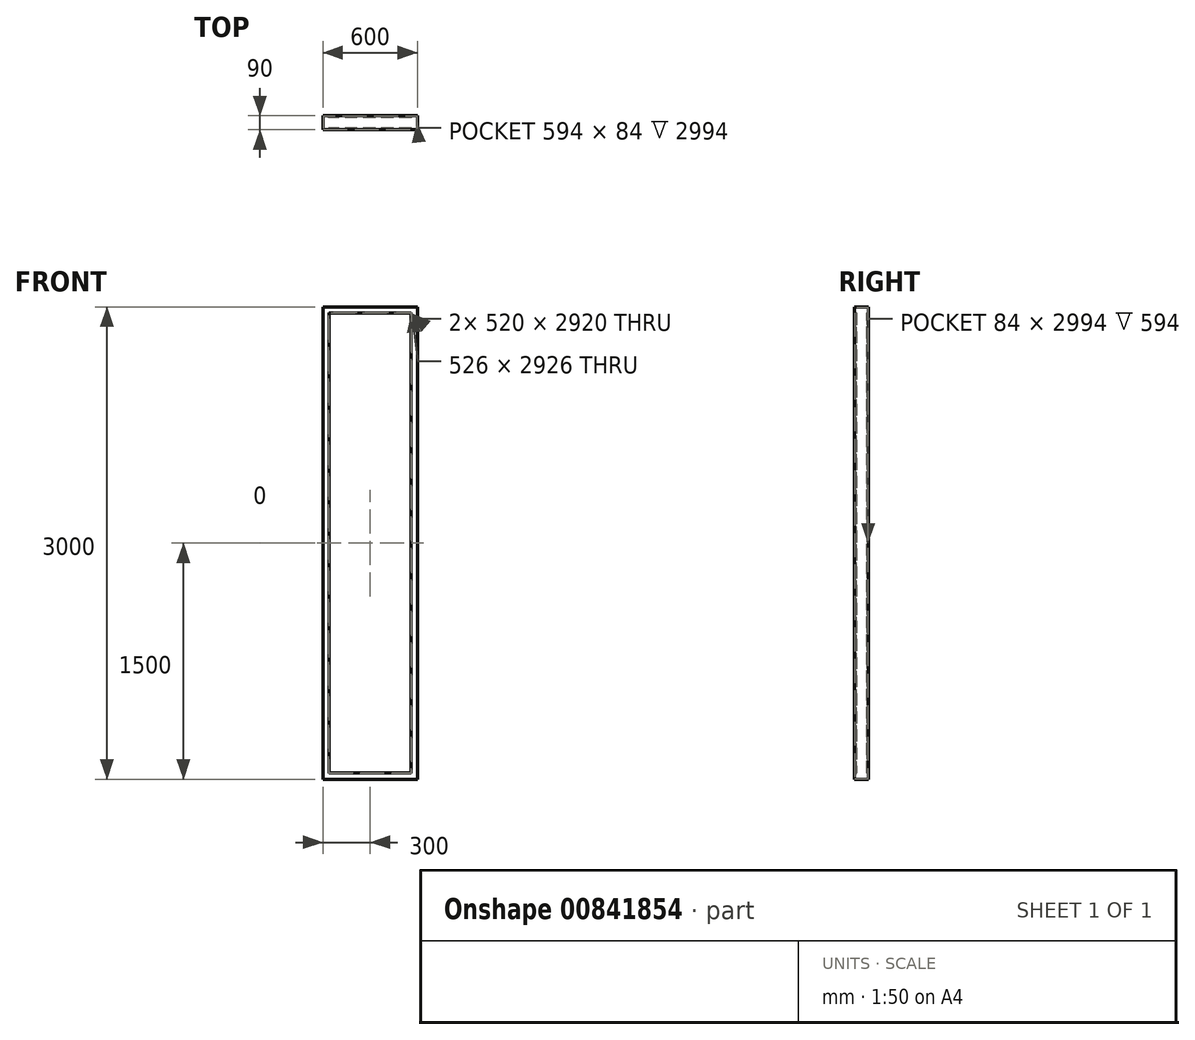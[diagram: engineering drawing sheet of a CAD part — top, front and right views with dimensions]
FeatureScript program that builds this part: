
annotation { "Feature Type Name" : "Feature", "Feature Type Description" : "" }
export const myFeature = defineFeature(function(context is Context, id is Id, definition is map)
    precondition{}
    {
        {
            var Q0;
            Q0=qCreatedBy(makeId("Front.planeOp"),FACE);
            var sketch = newSketch(context, id + "F0", { "sketchPlane" : qUnion([Q0])});
            skLineSegment(sketch, "E0.bottom", {"start": v(0, 0) * mm, "end": v(600, 0) * mm});
            skLineSegment(sketch, "E0.top", {"start": v(0, 3000) * mm, "end": v(600, 3000) * mm});
            skLineSegment(sketch, "E0.left", {"start": v(0, 0) * mm, "end": v(0, 3000) * mm});
            skLineSegment(sketch, "E0.right", {"start": v(600, 0) * mm, "end": v(600, 3000) * mm});
            skSolve(sketch);
        }
        {
            var Q0;
            Q0=qCreatedBy(makeId("Top.planeOp"),FACE);
            var sketch = newSketch(context, id + "F1", { "sketchPlane" : qUnion([Q0])});
            skLineSegment(sketch, "E1", {"start": v(0, 0) * mm, "end": v(0, -45) * mm});
            skLineSegment(sketch, "E2", {"start": v(0, -45) * mm, "end": v(40, -45) * mm});
            skLineSegment(sketch, "E3", {"start": v(40, -45) * mm, "end": v(40, -33) * mm});
            skLineSegment(sketch, "E4.MirrorCS", {"start": v(0, 0) * mm, "end": v(0, 45) * mm});
            skLineSegment(sketch, "E5.MirrorCS", {"start": v(0, 45) * mm, "end": v(40, 45) * mm});
            skLineSegment(sketch, "E6.MirrorCS", {"start": v(40, 45) * mm, "end": v(40, 33) * mm});
            skLineSegment(sketch, "E7.0", {"start": v(37, 42) * mm, "end": v(37, 33) * mm});
            skLineSegment(sketch, "E7.1", {"start": v(3, 42) * mm, "end": v(37, 42) * mm});
            skLineSegment(sketch, "E7.2", {"start": v(37, -42) * mm, "end": v(37, -33) * mm});
            skLineSegment(sketch, "E7.3", {"start": v(3, -42) * mm, "end": v(37, -42) * mm});
            skLineSegment(sketch, "E7.4", {"start": v(3, 0) * mm, "end": v(3, -42) * mm});
            skLineSegment(sketch, "E7.5", {"start": v(3, 0) * mm, "end": v(3, 42) * mm});
            skLineSegment(sketch, "E8", {"start": v(37, 33) * mm, "end": v(40, 33) * mm});
            skLineSegment(sketch, "E9", {"start": v(37, -33) * mm, "end": v(40, -33) * mm});
            skSolve(sketch);
        }
        {
            var Q0;
            Q0=qSketchRegion(id+"F1",true);
            var Q1;
            Q1=qConstructionFilter(qBodyType(qCreatedBy(id+"F0",EDGE),BodyType.WIRE),ConstructionObject.NO);
            sweep(context, id + "F2", {"profiles" : qUnion([Q0]), "path" : qUnion([Q1])});
        }
    });
